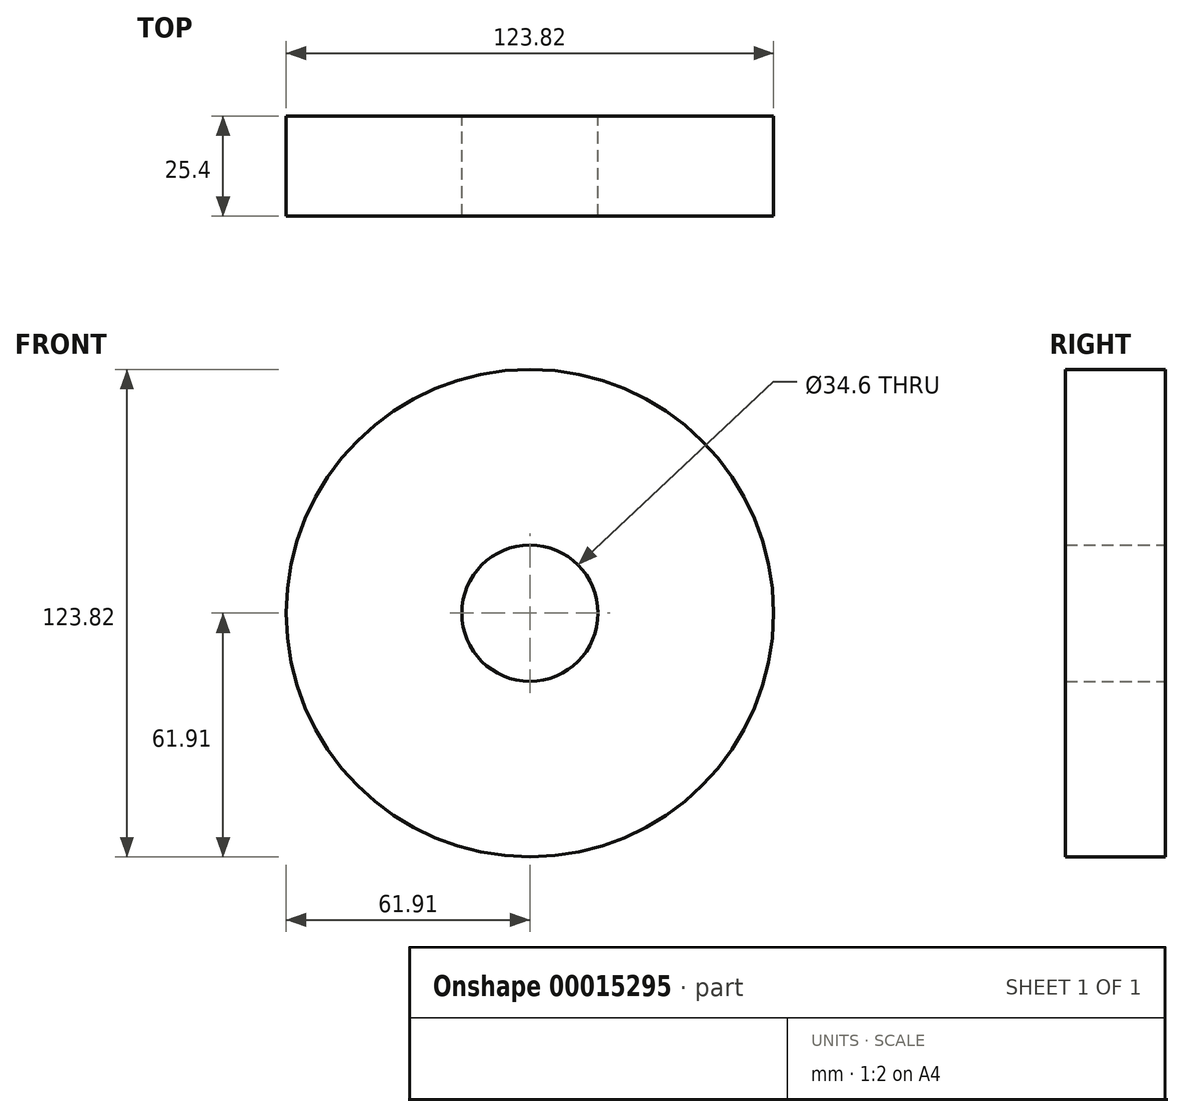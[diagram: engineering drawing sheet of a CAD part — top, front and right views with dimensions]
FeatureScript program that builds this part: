
annotation { "Feature Type Name" : "Feature", "Feature Type Description" : "" }
export const myFeature = defineFeature(function(context is Context, id is Id, definition is map)
    precondition{}
    {
        {
            var Q0;
            Q0=qCreatedBy(makeId("Front.planeOp"),FACE);
            var sketch = newSketch(context, id + "F0", { "sketchPlane" : qUnion([Q0])});
            skCircle(sketch, "E0", {"center": v(0, 0) * mm, "radius": 61.91 * mm});
            skCircle(sketch, "E1", {"center": v(0, 0) * mm, "radius": 17.3 * mm});
            skSolve(sketch);
        }
        {
            var Q0;
            Q0=makeQuery(id+"F0.imprint","IMPRINT",FACE,{"disambiguationData":[TD([[makeQuery(id+"F0.imprint","IMPRINT",EDGE,{"derivedFrom":sQuery(id+"F0.wireOp",EDGE,"E0")}),1.0]])]});
            extrude(context, id + "F1", {"entities" : qUnion([Q0]), "depth" : 25.4 * mm});
        }
    });
